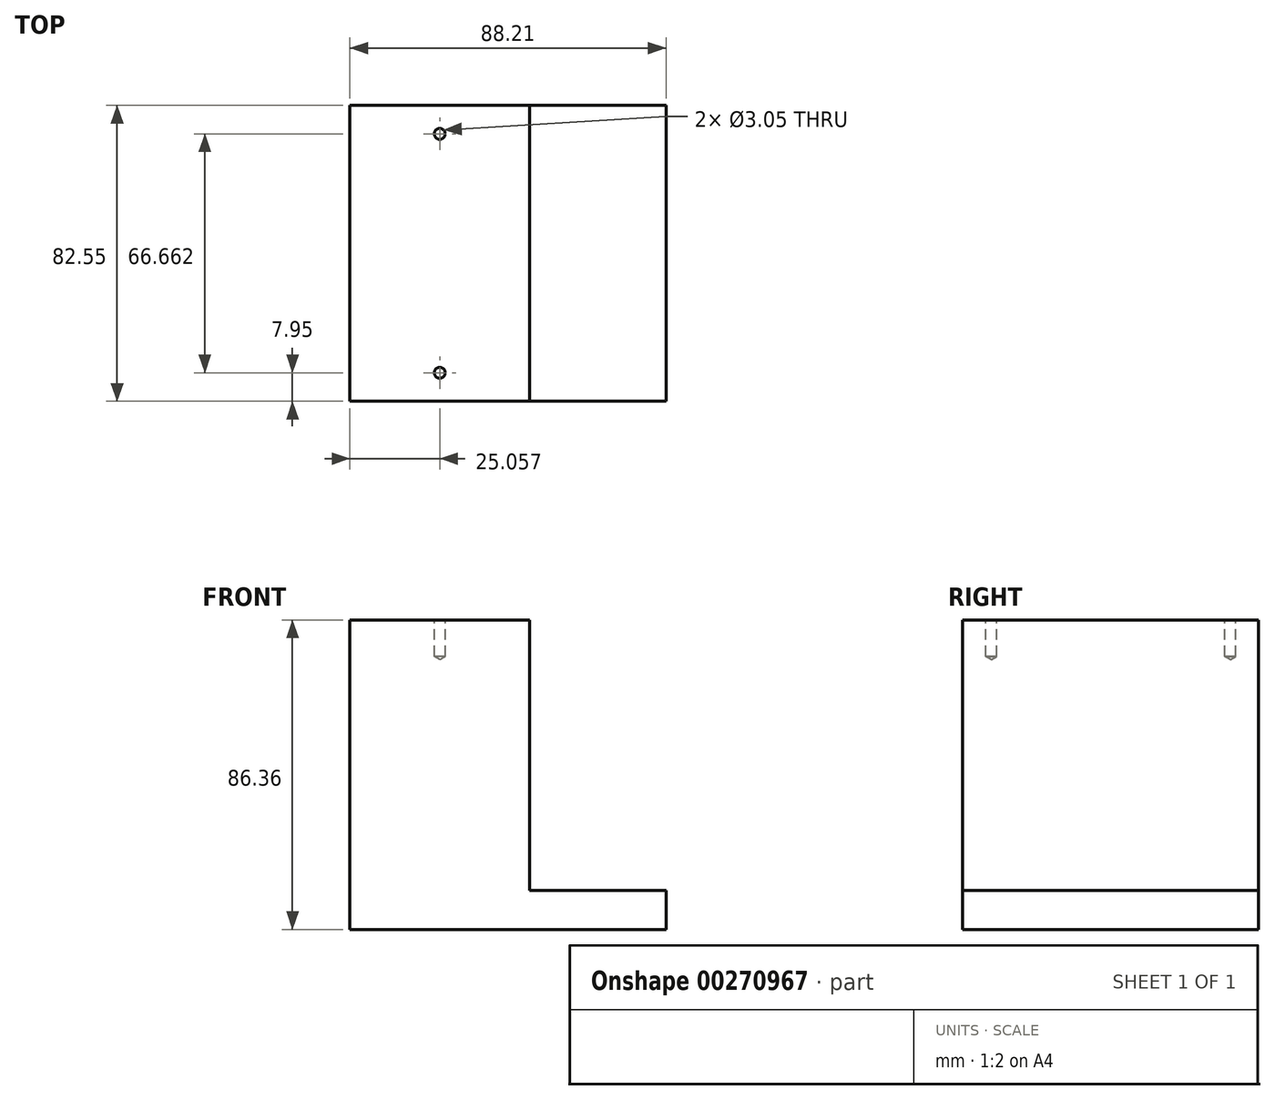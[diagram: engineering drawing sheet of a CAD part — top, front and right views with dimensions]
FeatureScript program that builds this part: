
annotation { "Feature Type Name" : "Feature", "Feature Type Description" : "" }
export const myFeature = defineFeature(function(context is Context, id is Id, definition is map)
    precondition{}
    {
        {
            var Q0;
            Q0=qCreatedBy(makeId("Front.planeOp"),FACE);
            var sketch = newSketch(context, id + "F0", { "sketchPlane" : qUnion([Q0])});
            skLineSegment(sketch, "E0", {"start": v(0, 0) * mm, "end": v(88.21, 0) * mm});
            skLineSegment(sketch, "E1", {"start": v(88.21, 0) * mm, "end": v(88.21, 10.86) * mm});
            skLineSegment(sketch, "E2", {"start": v(88.21, 10.86) * mm, "end": v(50.11, 10.86) * mm});
            skLineSegment(sketch, "E3", {"start": v(0, 0) * mm, "end": v(0, 88.9) * mm});
            skLineSegment(sketch, "E4", {"start": v(0, 88.9) * mm, "end": v(50.11, 88.9) * mm});
            skLineSegment(sketch, "E5", {"start": v(50.11, 88.9) * mm, "end": v(50.11, 10.86) * mm});
            skSolve(sketch);
        }
        {
            var Q0;
            Q0 = qSketchRegion(id + "F0", true);
            extrude(context, id + "F1", {"entities" : qUnion([Q0]), "depth" : 82.55 * mm});
        }
        {
            var Q0;
            Q0=makeQuery(id+"F1.opExtrude","SWEPT_FACE",FACE,{"disambiguationData":[OSD([sQuery(id+"F0.wireOp",EDGE,"E4")])]});
            var sketch = newSketch(context, id + "F2", { "sketchPlane" : qUnion([Q0])});
            skLineSegment(sketch, "E6.0", {"start": v(0, 0) * mm, "end": v(50.11, 0) * mm});
            skLineSegment(sketch, "E7.0", {"start": v(0, -82.55) * mm, "end": v(50.11, -82.55) * mm});
            skLineSegment(sketch, "E8.0", {"start": v(0, -82.55) * mm, "end": v(0, 0) * mm});
            skLineSegment(sketch, "E9.0", {"start": v(50.11, -82.55) * mm, "end": v(50.11, 0) * mm});
            skPoint(sketch, "E10", {"position": v(25.06, -7.94) * mm});
            skLineSegment(sketch, "E11", {"start": v(25.06, -7.94) * mm, "end": v(25.06, 0) * mm});
            skLineSegment(sketch, "E12", {"start": v(25.06, -82.55) * mm, "end": v(25.06, -74.6) * mm});
            skPoint(sketch, "E13", {"position": v(25.06, -74.6) * mm});
            skSolve(sketch);
        }
        {
            var Q0;
            Q0=sQuery(id+"F2.wireOp",VERTEX,"E10");
            var Q1;
            Q1=sQuery(id+"F2.wireOp",VERTEX,"E13");
            var Q2;
            Q2=makeQuery(id+"F1.opExtrude","SWEPT_BODY",BODY,{"disambiguationData":[OSD([sQuery(id+"F0.wireOp",EDGE,"E0"),sQuery(id+"F0.wireOp",EDGE,"E1"),sQuery(id+"F0.wireOp",EDGE,"E2"),sQuery(id+"F0.wireOp",EDGE,"E3"),sQuery(id+"F0.wireOp",EDGE,"E4"),sQuery(id+"F0.wireOp",EDGE,"E5")])]});
            hole(context, id + "F3", {"style" : HoleStyle.C_BORE, "endStyle" : HoleEndStyle.BLIND, "holeDiameter" : 3.05 * mm, "cBoreDiameter" : 381 * mm, "cBoreDepth" : 2.54 * mm, "holeDepth" : 12.7 * mm, "tappedDepth" : 12.7 * mm, "tapClearance" : 3, "locations" : qUnion([Q0, Q1]), "scope" : qUnion([Q2])});
        }
    });
